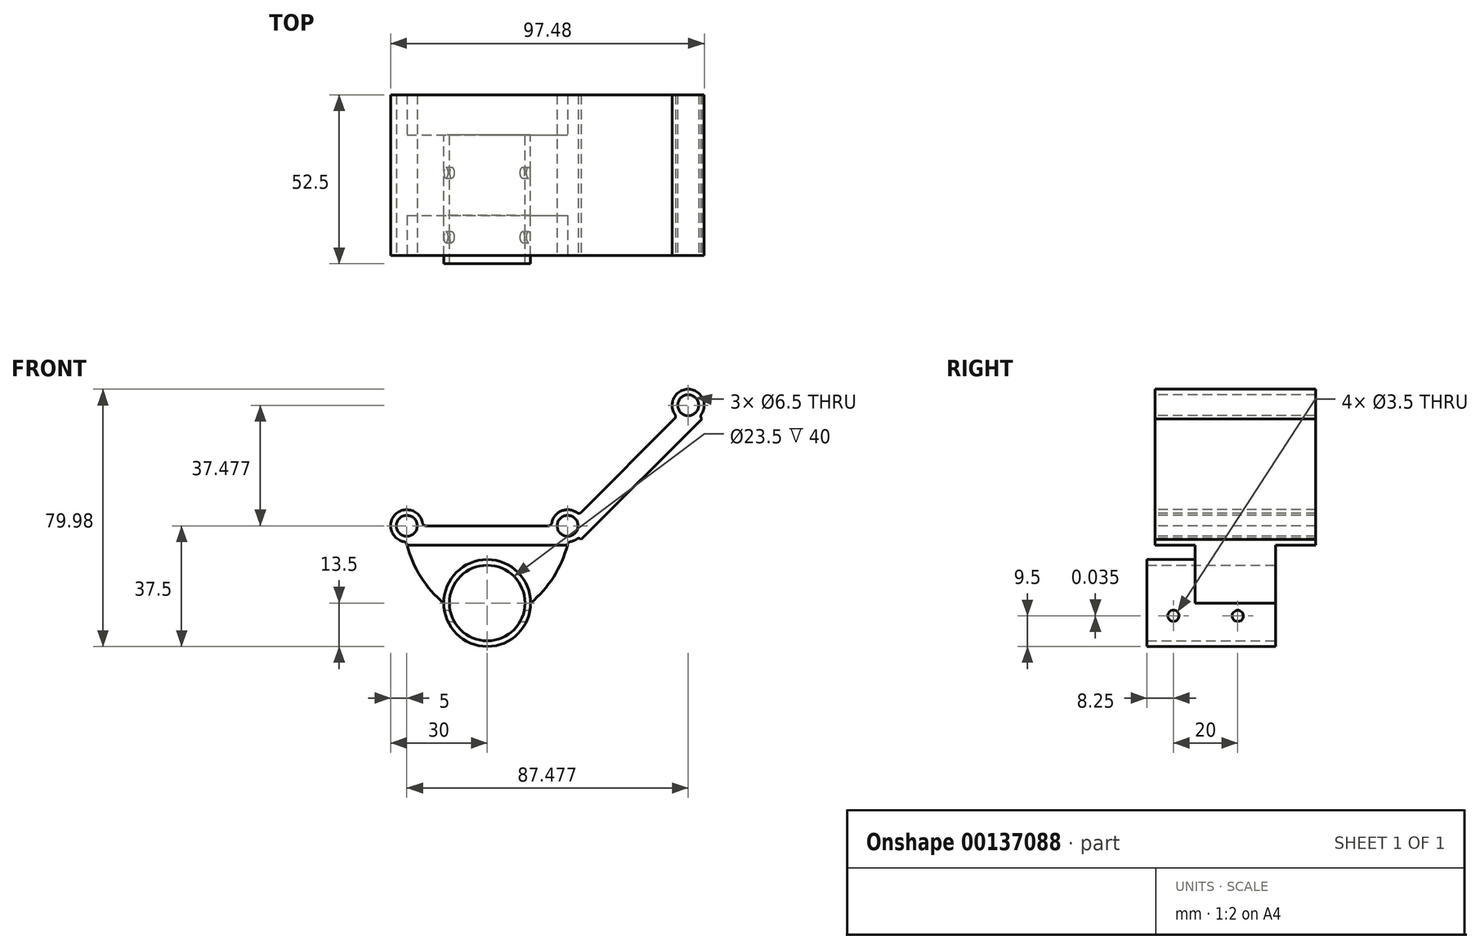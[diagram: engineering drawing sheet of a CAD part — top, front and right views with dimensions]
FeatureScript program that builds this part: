
annotation { "Feature Type Name" : "Feature", "Feature Type Description" : "" }
export const myFeature = defineFeature(function(context is Context, id is Id, definition is map)
    precondition{}
    {
        {
            var Q0;
            Q0=qCreatedBy(makeId("Front.planeOp"),FACE);
            var sketch = newSketch(context, id + "F0", { "sketchPlane" : qUnion([Q0])});
            skLineSegment(sketch, "E0", {"start": v(-50, 0) * mm, "end": v(0, 0) * mm, "construction": true});
            skLineSegment(sketch, "E1.right", {"start": v(-50, 0) * mm, "end": v(0, 0) * mm});
            skLineSegment(sketch, "E2.top", {"start": v(-50, -6) * mm, "end": v(0, -6) * mm});
            skLineSegment(sketch, "E2.left", {"start": v(-50, 0) * mm, "end": v(-50, -6) * mm});
            skLineSegment(sketch, "E2.right", {"start": v(0, 0) * mm, "end": v(0, -6) * mm});
            skLineSegment(sketch, "E3.bottom", {"start": v(0, 0) * mm, "end": v(4.24, -4.24) * mm});
            skLineSegment(sketch, "E3.top", {"start": v(37.48, 37.48) * mm, "end": v(41.72, 33.23) * mm});
            skLineSegment(sketch, "E3.left", {"start": v(0, 0) * mm, "end": v(37.48, 37.48) * mm});
            skLineSegment(sketch, "E3.right", {"start": v(4.24, -4.24) * mm, "end": v(41.72, 33.23) * mm});
            skPoint(sketch, "E4", {"position": v(0, 0) * mm});
            skCircle(sketch, "E5", {"center": v(-50, 0) * mm, "radius": 5 * mm});
            skCircle(sketch, "E6", {"center": v(0, 0) * mm, "radius": 5 * mm});
            skCircle(sketch, "E7", {"center": v(37.48, 37.48) * mm, "radius": 5 * mm});
            skSolve(sketch);
        }
        {
            var Q0;
            Q0 = qSketchRegion(id + "F0", true);
            extrude(context, id + "F1", {"entities" : qUnion([Q0]), "oppositeDirection" : true, "depth" : 50 * mm});
        }
        {
            var Q0;
            Q0=makeQuery(id+"F1.opExtrude","SWEPT_EDGE",EDGE,{"disambiguationData":[OSD([sQuery(id+"F0.wireOp",EDGE,"E3.left"),sQuery(id+"F0.wireOp",EDGE,"E7")])]});
            var Q1;
            Q1=makeQuery(id+"F1.opExtrude","SWEPT_EDGE",EDGE,{"disambiguationData":[OSD([sQuery(id+"F0.wireOp",EDGE,"E3.left"),sQuery(id+"F0.wireOp",EDGE,"E6")])]});
            var Q2;
            Q2=makeQuery(id+"F1.opExtrude","SWEPT_EDGE",EDGE,{"disambiguationData":[OSD([sQuery(id+"F0.wireOp",EDGE,"E1.right"),sQuery(id+"F0.wireOp",EDGE,"E6")])]});
            var Q3;
            Q3=makeQuery(id+"F1.opExtrude","SWEPT_EDGE",EDGE,{"disambiguationData":[OSD([sQuery(id+"F0.wireOp",EDGE,"E1.right"),sQuery(id+"F0.wireOp",EDGE,"E5")])]});
            var Q4;
            Q4=makeQuery(id+"F1.opExtrude","SWEPT_EDGE",EDGE,{"disambiguationData":[OSD([sQuery(id+"F0.wireOp",EDGE,"E3.top"),sQuery(id+"F0.wireOp",EDGE,"E7")])]});
            var Q5;
            Q5=makeQuery(id+"F1.opExtrude","SWEPT_EDGE",EDGE,{"disambiguationData":[OSD([sQuery(id+"F0.wireOp",EDGE,"E3.bottom"),sQuery(id+"F0.wireOp",EDGE,"E6")])]});
            var Q6;
            Q6=makeQuery(id+"F1.opExtrude","SWEPT_EDGE",EDGE,{"disambiguationData":[OSD([sQuery(id+"F0.wireOp",EDGE,"E2.right"),sQuery(id+"F0.wireOp",EDGE,"E6")])]});
            var Q7;
            Q7=makeQuery(id+"F1.opExtrude","SWEPT_EDGE",EDGE,{"disambiguationData":[OSD([sQuery(id+"F0.wireOp",EDGE,"E2.left"),sQuery(id+"F0.wireOp",EDGE,"E5")])]});
            fillet(context, id + "F2", {"entities" : qUnion([Q0, Q1, Q2, Q3, Q4, Q5, Q6, Q7]), "radius" : 1 * mm, "tangentPropagation" : true, "allowEdgeOverflow" : false});
        }
        {
            var Q0;
            Q0=makeQuery(id+"F1.opExtrude","CAP_FACE",FACE,{"disambiguationData":[OSD([sQuery(id+"F0.wireOp",EDGE,"E1.right"),sQuery(id+"F0.wireOp",EDGE,"E2.top"),sQuery(id+"F0.wireOp",EDGE,"E2.left"),sQuery(id+"F0.wireOp",EDGE,"E2.right"),sQuery(id+"F0.wireOp",EDGE,"E3.bottom"),sQuery(id+"F0.wireOp",EDGE,"E3.top"),sQuery(id+"F0.wireOp",EDGE,"E3.left"),sQuery(id+"F0.wireOp",EDGE,"E3.right"),sQuery(id+"F0.wireOp",EDGE,"E5"),sQuery(id+"F0.wireOp",EDGE,"E6"),sQuery(id+"F0.wireOp",EDGE,"E7")])],"isStart":true});
            var sketch = newSketch(context, id + "F3", { "sketchPlane" : qUnion([Q0])});
            skCircle(sketch, "E8", {"center": v(-50, 0) * mm, "radius": 3.25 * mm});
            skCircle(sketch, "E9", {"center": v(0, 0) * mm, "radius": 3.25 * mm});
            skCircle(sketch, "E10", {"center": v(37.48, 37.48) * mm, "radius": 3.25 * mm});
            skSolve(sketch);
        }
        {
            var Q0;
            Q0 = qSketchRegion(id + "F3", true);
            extrude(context, id + "F4", {"entities" : qUnion([Q0]), "operationType" : NewBodyOperationType.REMOVE, "endBound" : BoundingType.THROUGH_ALL, "oppositeDirection" : true, "depth" : 25 * mm});
        }
        {
            var Q0;
            Q0=makeQuery(id+"F1.opExtrude","SWEPT_FACE",FACE,{"disambiguationData":[OSD([sQuery(id+"F0.wireOp",EDGE,"E2.top")])]});
            var sketch = newSketch(context, id + "F5", { "sketchPlane" : qUnion([Q0])});
            skLineSegment(sketch, "E11.bottom", {"start": v(-50, -12.5) * mm, "end": v(0, -12.5) * mm});
            skLineSegment(sketch, "E11.top", {"start": v(-50, -37.5) * mm, "end": v(0, -37.5) * mm});
            skLineSegment(sketch, "E11.left", {"start": v(-50, -12.5) * mm, "end": v(-50, -37.5) * mm});
            skLineSegment(sketch, "E11.right", {"start": v(0, -12.5) * mm, "end": v(0, -37.5) * mm});
            skSolve(sketch);
        }
        {
            var Q0;
            Q0 = qSketchRegion(id + "F5", true);
            extrude(context, id + "F6", {"entities" : qUnion([Q0]), "operationType" : NewBodyOperationType.ADD, "depth" : 18 * mm});
        }
        {
            var Q0;
            Q0=makeQuery(id+"F6.opExtrude","SWEPT_FACE",FACE,{"disambiguationData":[OSD([sQuery(id+"F5.wireOp",EDGE,"E11.top")])]});
            var sketch = newSketch(context, id + "F7", { "sketchPlane" : qUnion([Q0])});
            skCircle(sketch, "E12", {"center": v(25, -24) * mm, "radius": 13.5 * mm});
            skSolve(sketch);
        }
        {
            var Q0;
            Q0 = qSketchRegion(id + "F7", true);
            extrude(context, id + "F8", {"entities" : qUnion([Q0]), "operationType" : NewBodyOperationType.ADD, "oppositeDirection" : true, "depth" : 40 * mm});
        }
        {
            var Q0;
            Q0=makeQuery(id+"F8.boolean.opBoolean","MERGE",FACE,{"derivedFrom":[makeQuery(id+"F6.opExtrude","SWEPT_FACE",FACE,{"disambiguationData":[OSD([sQuery(id+"F5.wireOp",EDGE,"E11.top")])]}),makeQuery(id+"F8.opExtrude","CAP_FACE",FACE,{"disambiguationData":[OSD([sQuery(id+"F7.wireOp",EDGE,"E12")])],"isStart":true})]});
            var sketch = newSketch(context, id + "F9", { "sketchPlane" : qUnion([Q0])});
            skCircle(sketch, "E13", {"center": v(25, -24) * mm, "radius": 11.75 * mm});
            skSolve(sketch);
        }
        {
            var Q0;
            Q0 = qSketchRegion(id + "F9", true);
            extrude(context, id + "F10", {"entities" : qUnion([Q0]), "operationType" : NewBodyOperationType.REMOVE, "endBound" : BoundingType.THROUGH_ALL, "oppositeDirection" : true, "depth" : 25 * mm});
        }
        {
            var Q0;
            Q0=makeQuery(id+"F6.boolean.opBoolean","MERGE",FACE,{"derivedFrom":[makeQuery(id+"F1.opExtrude","SWEPT_FACE",FACE,{"disambiguationData":[OSD([sQuery(id+"F0.wireOp",EDGE,"E2.right")])]}),makeQuery(id+"F6.opExtrude","SWEPT_FACE",FACE,{"disambiguationData":[OSD([sQuery(id+"F5.wireOp",EDGE,"E11.right")])]})]});
            var sketch = newSketch(context, id + "F11", { "sketchPlane" : qUnion([Q0])});
            skCircle(sketch, "E14", {"center": v(25.75, -28) * mm, "radius": 1.75 * mm});
            skCircle(sketch, "E15", {"center": v(5.75, -27.96) * mm, "radius": 1.75 * mm});
            skSolve(sketch);
        }
        {
            var Q0;
            Q0 = qSketchRegion(id + "F11", true);
            extrude(context, id + "F12", {"entities" : qUnion([Q0]), "operationType" : NewBodyOperationType.REMOVE, "endBound" : BoundingType.THROUGH_ALL, "oppositeDirection" : true, "depth" : 25 * mm});
        }
        {
            var Q0;
            Q0=makeQuery(id+"F6.opExtrude","CAP_EDGE",EDGE,{"disambiguationData":[OSD([sQuery(id+"F5.wireOp",EDGE,"E11.right")])],"isStart":false});
            fillet(context, id + "F13", {"entities" : qUnion([Q0]), "radius" : 35 * mm, "tangentPropagation" : true, "allowEdgeOverflow" : false});
        }
        {
            var Q0;
            Q0=makeQuery(id+"F6.opExtrude","CAP_EDGE",EDGE,{"disambiguationData":[OSD([sQuery(id+"F5.wireOp",EDGE,"E11.left")])],"isStart":false});
            fillet(context, id + "F14", {"entities" : qUnion([Q0]), "radius" : 35 * mm, "tangentPropagation" : true, "allowEdgeOverflow" : false});
        }
    });
